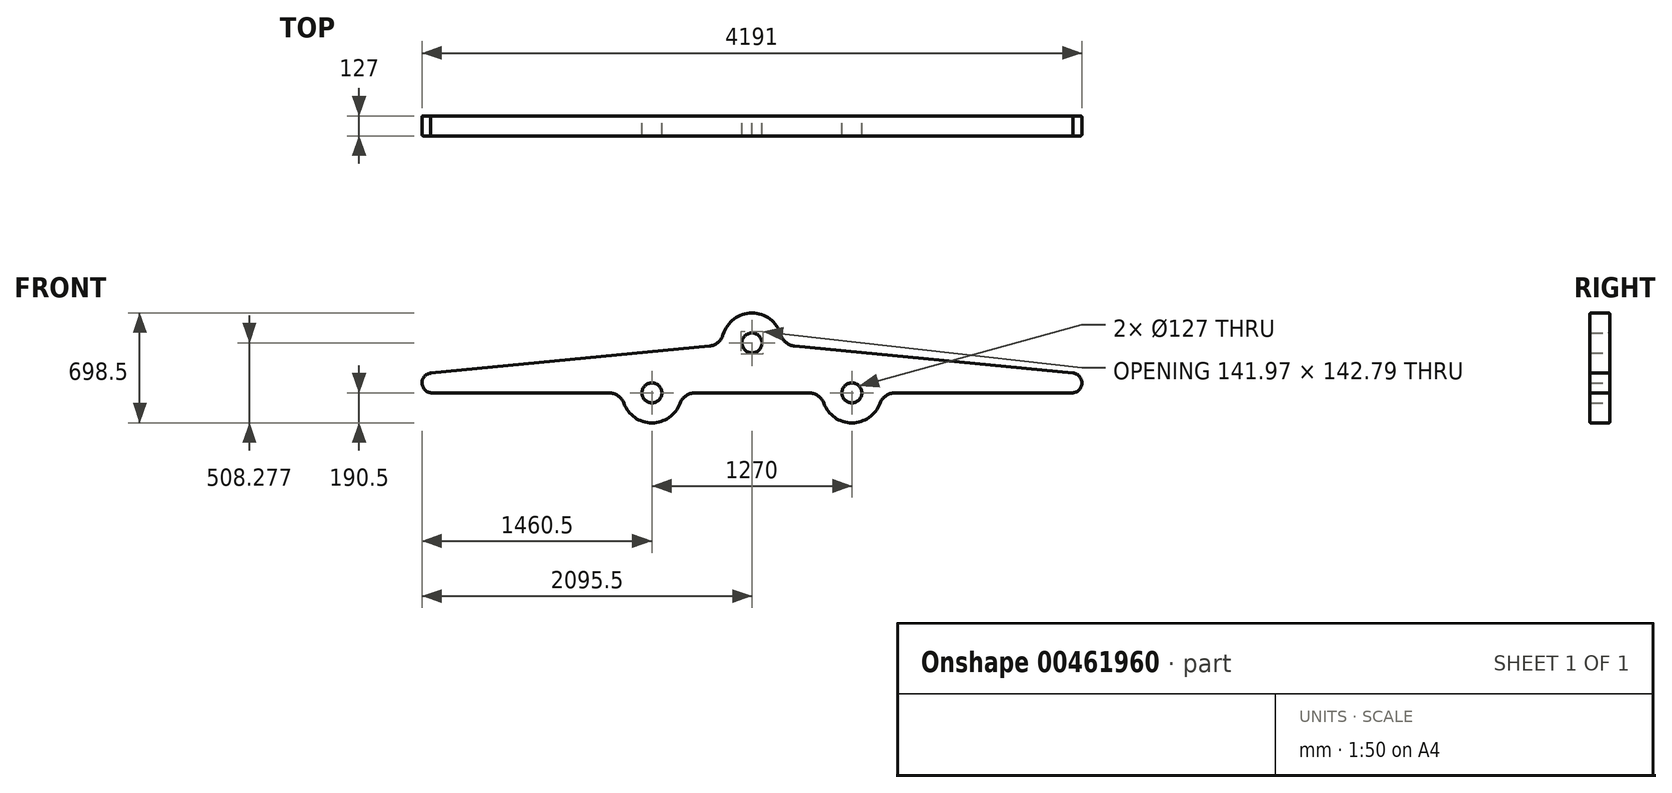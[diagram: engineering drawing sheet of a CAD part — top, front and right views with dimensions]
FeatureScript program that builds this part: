
annotation { "Feature Type Name" : "Feature", "Feature Type Description" : "" }
export const myFeature = defineFeature(function(context is Context, id is Id, definition is map)
    precondition{}
    {
        {
            var Q0;
            Q0=qCreatedBy(makeId("Front.planeOp"),FACE);
            var sketch = newSketch(context, id + "F0", { "sketchPlane" : qUnion([Q0])});
            skCircle(sketch, "E0", {"center": v(0, 254) * mm, "radius": 63.5 * mm});
            skArc(sketch, "E1", {"start": v(2032, -63.5) * mm, "mid": v(2095.38, -3.95) * mm, "end": v(2039.88, 63) * mm});
            skArc(sketch, "E2", {"start": v(-2039.88, 63) * mm, "mid": v(-2095.38, -3.95) * mm, "end": v(-2032, -63.5) * mm});
            skLineSegment(sketch, "E3", {"start": v(-7.88, 317) * mm, "end": v(0, 318) * mm});
            skLineSegment(sketch, "E4", {"start": v(0, 318) * mm, "end": v(7.88, 317) * mm});
            skLineSegment(sketch, "E5", {"start": v(-2032, -63.5) * mm, "end": v(-908.86, -63.5) * mm});
            skLineSegment(sketch, "E6", {"start": v(-40.81, 254) * mm, "end": v(-63.5, 254) * mm, "construction": true});
            skLineSegment(sketch, "E7", {"start": v(-270.85, 233.96) * mm, "end": v(-2039.88, 63) * mm});
            skPoint(sketch, "E7.startSnap0", {"position": v(-40.81, 254) * mm});
            skLineSegment(sketch, "E8", {"start": v(270.85, 233.96) * mm, "end": v(2039.88, 63) * mm});
            skCircle(sketch, "E9", {"center": v(-635, -63.5) * mm, "radius": 63.5 * mm});
            skCircle(sketch, "E10", {"center": v(635, -63.5) * mm, "radius": 63.5 * mm});
            skPoint(sketch, "E11.orphan", {"position": v(-1749.57, 254) * mm});
            skPoint(sketch, "E12.orphan", {"position": v(1667.95, 254) * mm});
            skArc(sketch, "E13.0", {"start": v(-813.6, -129.76) * mm, "mid": v(-635, -254) * mm, "end": v(-456.4, -129.76) * mm});
            skArc(sketch, "E14.0", {"start": v(456.4, -129.76) * mm, "mid": v(635, -254) * mm, "end": v(813.6, -129.76) * mm});
            skLineSegment(sketch, "E15.trimOffspring", {"start": v(908.86, -63.5) * mm, "end": v(2032, -63.5) * mm});
            skLineSegment(sketch, "E16.trimOffspring", {"start": v(-361.14, -63.5) * mm, "end": v(361.14, -63.5) * mm});
            skPoint(sketch, "E17.visualSharp", {"position": v(-825.5, -63.5) * mm});
            skArc(sketch, "E17.filletArc", {"start": v(-813.6, -129.76) * mm, "mid": v(-850.84, -81.7) * mm, "end": v(-908.86, -63.5) * mm});
            skPoint(sketch, "E18.visualSharp", {"position": v(-444.5, -63.5) * mm});
            skArc(sketch, "E18.filletArc", {"start": v(-361.14, -63.5) * mm, "mid": v(-419.16, -81.7) * mm, "end": v(-456.4, -129.76) * mm});
            skPoint(sketch, "E19.visualSharp", {"position": v(444.5, -63.5) * mm});
            skArc(sketch, "E19.filletArc", {"start": v(456.4, -129.76) * mm, "mid": v(419.16, -81.7) * mm, "end": v(361.14, -63.5) * mm});
            skPoint(sketch, "E20.visualSharp", {"position": v(825.5, -63.5) * mm});
            skArc(sketch, "E20.filletArc", {"start": v(908.86, -63.5) * mm, "mid": v(850.84, -81.7) * mm, "end": v(813.6, -129.76) * mm});
            skArc(sketch, "E21.0", {"start": v(183.01, 306.89) * mm, "mid": v(0, 444.5) * mm, "end": v(-183.01, 306.89) * mm});
            skPoint(sketch, "E22.visualSharp", {"position": v(-190.1, 241.77) * mm});
            skArc(sketch, "E22.filletArc", {"start": v(-270.85, 233.96) * mm, "mid": v(-215.72, 256.92) * mm, "end": v(-183.01, 306.89) * mm});
            skPoint(sketch, "E23.visualSharp", {"position": v(190.1, 241.77) * mm});
            skArc(sketch, "E23.filletArc", {"start": v(183.01, 306.89) * mm, "mid": v(215.72, 256.92) * mm, "end": v(270.85, 233.96) * mm});
            skSolve(sketch);
        }
        {
            var Q0;
            Q0=makeQuery(id+"F0.imprint","IMPRINT",FACE,{"disambiguationData":[TD([[makeQuery(id+"F0.imprint","IMPRINT",EDGE,{"derivedFrom":sQuery(id+"F0.wireOp",EDGE,"E1")}),1.0]])]});
            extrude(context, id + "F1", {"entities" : qUnion([Q0]), "endBound" : BoundingType.SYMMETRIC, "depth" : 127 * mm});
        }
        {
            var Q0;
            Q0=makeQuery(id+"F1.opExtrude","CAP_EDGE",EDGE,{"disambiguationData":[OSD([sQuery(id+"F0.wireOp",EDGE,"E7")])],"isStart":false});
            var Q1;
            Q1=makeQuery(id+"F1.opExtrude","CAP_EDGE",EDGE,{"disambiguationData":[OSD([sQuery(id+"F0.wireOp",EDGE,"E7")])],"isStart":true});
            var Q2;
            Q2=makeQuery(id+"F1.opExtrude","CAP_EDGE",EDGE,{"disambiguationData":[OSD([sQuery(id+"F0.wireOp",EDGE,"E0")])],"isStart":false});
            var Q3;
            Q3=makeQuery(id+"F1.opExtrude","CAP_EDGE",EDGE,{"disambiguationData":[OSD([sQuery(id+"F0.wireOp",EDGE,"E9")])],"isStart":false});
            var Q4;
            Q4=makeQuery(id+"F1.opExtrude","CAP_EDGE",EDGE,{"disambiguationData":[OSD([sQuery(id+"F0.wireOp",EDGE,"E10")])],"isStart":false});
            var Q5;
            Q5=makeQuery(id+"F1.opExtrude","CAP_EDGE",EDGE,{"disambiguationData":[OSD([sQuery(id+"F0.wireOp",EDGE,"E15.trimOffspring")])],"isStart":false});
            var Q6;
            Q6=makeQuery(id+"F1.opExtrude","CAP_EDGE",EDGE,{"disambiguationData":[OSD([sQuery(id+"F0.wireOp",EDGE,"E0")])],"isStart":true});
            var Q7;
            Q7=makeQuery(id+"F1.opExtrude","CAP_EDGE",EDGE,{"disambiguationData":[OSD([sQuery(id+"F0.wireOp",EDGE,"E10")])],"isStart":true});
            var Q8;
            Q8=makeQuery(id+"F1.opExtrude","CAP_EDGE",EDGE,{"disambiguationData":[OSD([sQuery(id+"F0.wireOp",EDGE,"E9")])],"isStart":true});
            var Q9;
            Q9=makeQuery(id+"F1.opExtrude","CAP_EDGE",EDGE,{"disambiguationData":[OSD([sQuery(id+"F0.wireOp",EDGE,"E5")])],"isStart":false});
            var Q10;
            Q10=makeQuery(id+"F1.opExtrude","CAP_EDGE",EDGE,{"disambiguationData":[OSD([sQuery(id+"F0.wireOp",EDGE,"E16.trimOffspring")])],"isStart":false});
            var Q11;
            Q11=makeQuery(id+"F1.opExtrude","CAP_EDGE",EDGE,{"disambiguationData":[OSD([sQuery(id+"F0.wireOp",EDGE,"E13.0")])],"isStart":true});
            fillet(context, id + "F2", {"entities" : qUnion([Q0, Q1, Q2, Q3, Q4, Q5, Q6, Q7, Q8, Q9, Q10, Q11]), "radius" : 7.62 * mm, "tangentPropagation" : true, "allowEdgeOverflow" : false});
        }
    });
